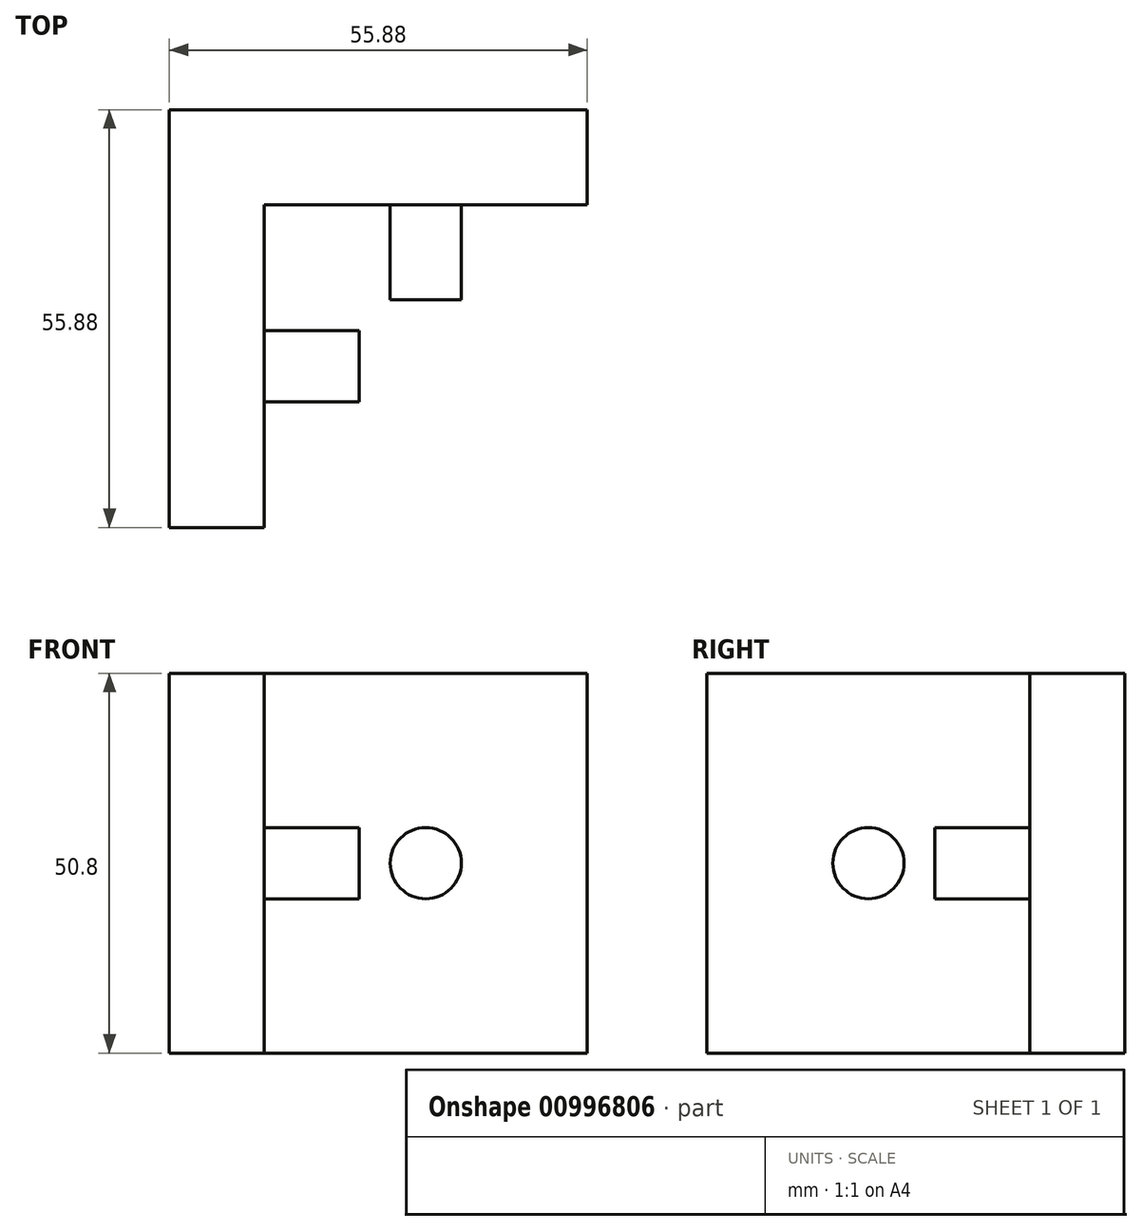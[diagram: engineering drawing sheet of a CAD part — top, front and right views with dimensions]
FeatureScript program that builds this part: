
annotation { "Feature Type Name" : "Feature", "Feature Type Description" : "" }
export const myFeature = defineFeature(function(context is Context, id is Id, definition is map)
    precondition{}
    {
        {
            var Q0;
            Q0=qCreatedBy(makeId("Top.planeOp"),FACE);
            var sketch = newSketch(context, id + "F0", { "sketchPlane" : qUnion([Q0])});
            skLineSegment(sketch, "E0", {"start": v(0, 0) * mm, "end": v(0, -55.88) * mm});
            skLineSegment(sketch, "E1", {"start": v(0, -55.88) * mm, "end": v(12.7, -55.88) * mm});
            skLineSegment(sketch, "E2", {"start": v(12.7, -55.88) * mm, "end": v(12.7, -12.7) * mm});
            skLineSegment(sketch, "E3", {"start": v(12.7, -12.7) * mm, "end": v(55.88, -12.7) * mm});
            skLineSegment(sketch, "E4", {"start": v(55.88, -12.7) * mm, "end": v(55.88, 0) * mm});
            skLineSegment(sketch, "E5", {"start": v(55.88, 0) * mm, "end": v(0, 0) * mm});
            skLineSegment(sketch, "E6", {"start": v(34.29, -12.7) * mm, "end": v(34.29, 0) * mm});
            skLineSegment(sketch, "E7", {"start": v(12.7, -34.29) * mm, "end": v(0, -34.29) * mm});
            skSolve(sketch);
        }
        {
            var Q0;
            Q0 = qSketchRegion(id + "F0", true);
            extrude(context, id + "F1", {"entities" : qUnion([Q0]), "depth" : 50.8 * mm, "offsetDistance" : 25.4 * mm});
        }
        {
            var Q0;
            Q0=makeQuery(id+"F1.opExtrude","SWEPT_FACE",FACE,{"disambiguationData":[OSD([sQuery(id+"F0.wireOp",EDGE,"E3")])]});
            var sketch = newSketch(context, id + "F2", { "sketchPlane" : qUnion([Q0])});
            skCircle(sketch, "E8", {"center": v(34.29, 25.4) * mm, "radius": 4.76 * mm});
            skLineSegment(sketch, "E9", {"start": v(34.29, 25.4) * mm, "end": v(34.29, 50.8) * mm, "construction": true});
            skLineSegment(sketch, "E10", {"start": v(34.29, 25.4) * mm, "end": v(34.29, 0) * mm, "construction": true});
            skSolve(sketch);
        }
        {
            var Q0;
            Q0 = qSketchRegion(id + "F2", true);
            extrude(context, id + "F3", {"entities" : qUnion([Q0]), "operationType" : NewBodyOperationType.ADD, "depth" : 12.7 * mm, "offsetDistance" : 25.4 * mm});
        }
        {
            var Q0;
            Q0=makeQuery(id+"F1.opExtrude","SWEPT_FACE",FACE,{"disambiguationData":[OSD([sQuery(id+"F0.wireOp",EDGE,"E2")])]});
            var sketch = newSketch(context, id + "F4", { "sketchPlane" : qUnion([Q0])});
            skCircle(sketch, "E11", {"center": v(-34.29, 25.4) * mm, "radius": 4.76 * mm});
            skLineSegment(sketch, "E12", {"start": v(-34.29, 25.4) * mm, "end": v(-34.3, 50.8) * mm, "construction": true});
            skLineSegment(sketch, "E13", {"start": v(-34.29, 25.4) * mm, "end": v(-34.29, 0) * mm, "construction": true});
            skSolve(sketch);
        }
        {
            var Q0;
            Q0 = qSketchRegion(id + "F4", true);
            extrude(context, id + "F5", {"entities" : qUnion([Q0]), "operationType" : NewBodyOperationType.ADD, "depth" : 12.7 * mm, "offsetDistance" : 25.4 * mm});
        }
    });
